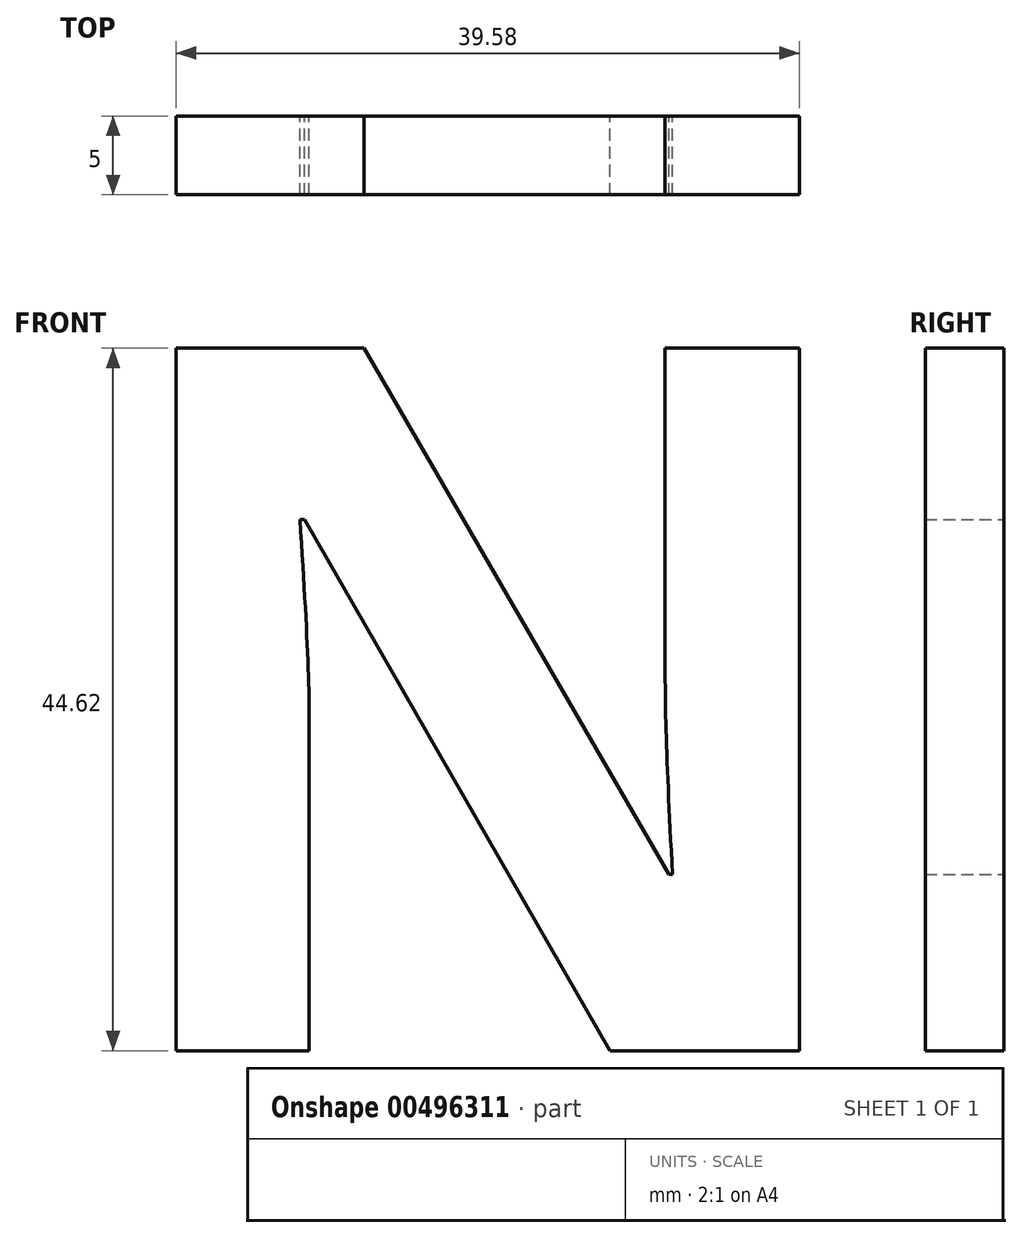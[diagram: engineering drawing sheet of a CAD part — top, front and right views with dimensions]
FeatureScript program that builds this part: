
annotation { "Feature Type Name" : "Feature", "Feature Type Description" : "" }
export const myFeature = defineFeature(function(context is Context, id is Id, definition is map)
    precondition{}
    {
        {
            var Q0;
            Q0=qCreatedBy(makeId("Front.planeOp"),FACE);
            var sketch = newSketch(context, id + "F0", { "sketchPlane" : qUnion([Q0])});
            skText(sketch, "E0", { "text": "N", "fontName": "OpenSans-Bold.ttf"});
            const initialGuessF0  = {"E0": [-0.07077, 0.02482, 1, 0, 0.045]};
            skSetInitialGuess(sketch, initialGuessF0);
            skSolve(sketch);
        }
        {
            var Q0;
            Q0 = qSketchRegion(id + "F0", true);
            extrude(context, id + "F1", {"entities" : qUnion([Q0]), "depth" : 5 * mm});
        }
    });
